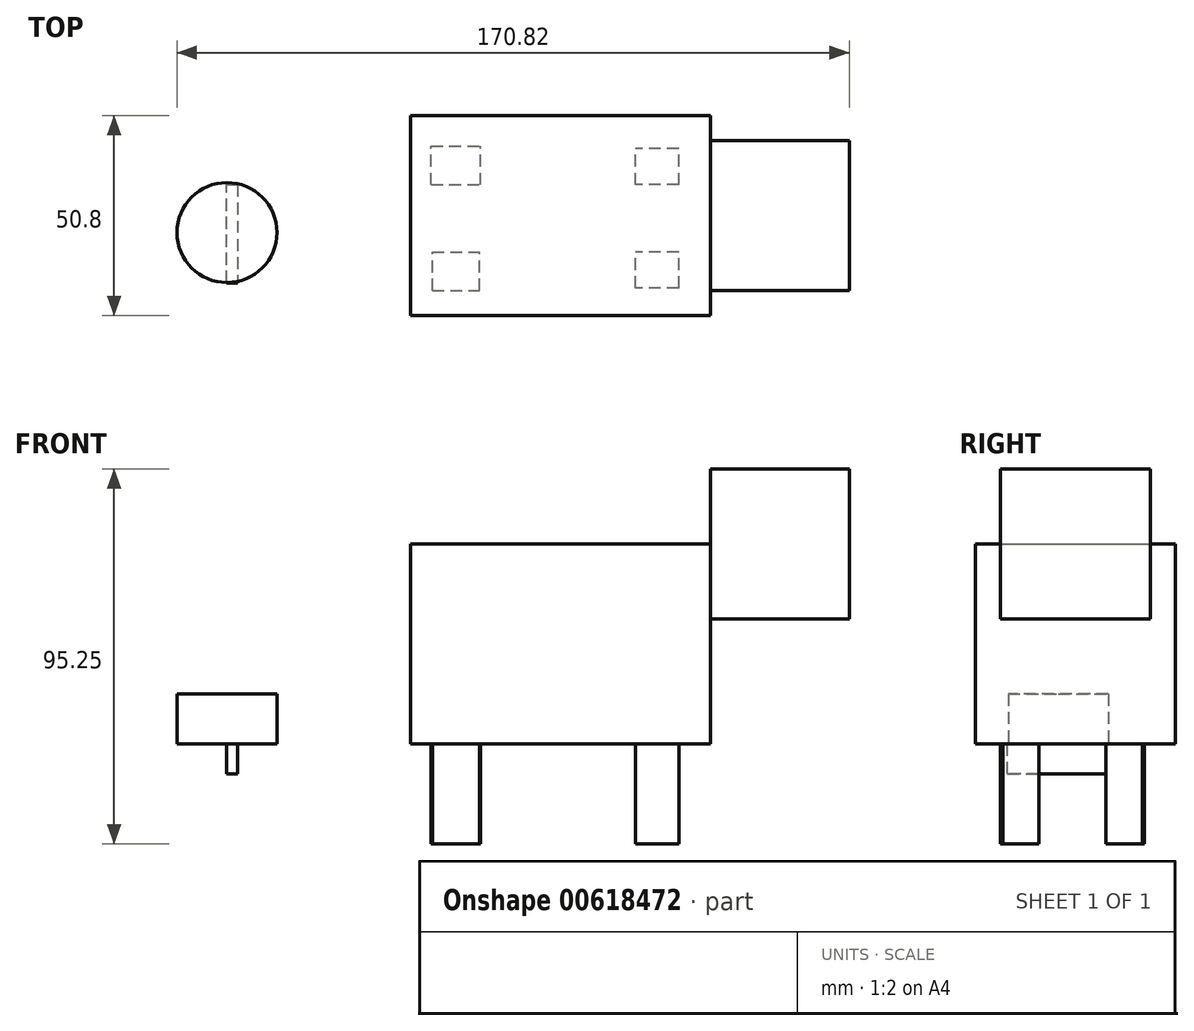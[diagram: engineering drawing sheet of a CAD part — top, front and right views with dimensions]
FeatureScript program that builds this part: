
annotation { "Feature Type Name" : "Feature", "Feature Type Description" : "" }
export const myFeature = defineFeature(function(context is Context, id is Id, definition is map)
    precondition{}
    {
        {
            var Q0;
            Q0=qCreatedBy(makeId("Front.planeOp"),FACE);
            var sketch = newSketch(context, id + "F0", { "sketchPlane" : qUnion([Q0])});
            skLineSegment(sketch, "E0.bottom", {"start": v(-11.56, 59.11) * mm, "end": v(64.64, 59.11) * mm});
            skLineSegment(sketch, "E0.top", {"start": v(-11.56, 8.31) * mm, "end": v(64.64, 8.31) * mm});
            skLineSegment(sketch, "E0.left", {"start": v(-11.56, 59.11) * mm, "end": v(-11.56, 8.31) * mm});
            skLineSegment(sketch, "E0.right", {"start": v(64.64, 59.11) * mm, "end": v(64.64, 8.31) * mm});
            skSolve(sketch);
        }
        {
            var Q0;
            Q0 = qSketchRegion(id + "F0", true);
            extrude(context, id + "F1", {"entities" : qUnion([Q0]), "depth" : 50.8 * mm, "offsetDistance" : 25.4 * mm});
        }
        {
            var Q0;
            Q0=makeQuery(id+"F1.opExtrude","SWEPT_FACE",FACE,{"disambiguationData":[OSD([sQuery(id+"F0.wireOp",EDGE,"E0.right")])]});
            var sketch = newSketch(context, id + "F2", { "sketchPlane" : qUnion([Q0])});
            skLineSegment(sketch, "E1.bottom", {"start": v(-6.35, 78.16) * mm, "end": v(-44.45, 78.16) * mm});
            skLineSegment(sketch, "E1.top", {"start": v(-6.35, 40.06) * mm, "end": v(-44.45, 40.06) * mm});
            skLineSegment(sketch, "E1.left", {"start": v(-6.35, 78.16) * mm, "end": v(-6.35, 40.06) * mm});
            skLineSegment(sketch, "E1.right", {"start": v(-44.45, 78.16) * mm, "end": v(-44.45, 40.06) * mm});
            skPoint(sketch, "E1.middle", {"position": v(-25.4, 59.11) * mm});
            skSolve(sketch);
        }
        {
            var Q0;
            Q0 = qSketchRegion(id + "F2", true);
            extrude(context, id + "F3", {"entities" : qUnion([Q0]), "operationType" : NewBodyOperationType.ADD, "depth" : 35.3 * mm, "offsetDistance" : 25.4 * mm});
        }
        {
            var Q0;
            Q0=makeQuery(id+"F1.opExtrude","SWEPT_FACE",FACE,{"disambiguationData":[OSD([sQuery(id+"F0.wireOp",EDGE,"E0.top")])]});
            var sketch = newSketch(context, id + "F4", { "sketchPlane" : qUnion([Q0])});
            skLineSegment(sketch, "E2.bottom", {"start": v(-6, 44.43) * mm, "end": v(6, 44.43) * mm});
            skLineSegment(sketch, "E2.top", {"start": v(-6, 34.66) * mm, "end": v(6, 34.66) * mm});
            skLineSegment(sketch, "E2.left", {"start": v(-6, 44.43) * mm, "end": v(-6, 34.66) * mm});
            skLineSegment(sketch, "E2.right", {"start": v(6, 44.43) * mm, "end": v(6, 34.66) * mm});
            skPoint(sketch, "E2.middle", {"position": v(0, 39.55) * mm});
            skLineSegment(sketch, "E3.bottom", {"start": v(-6.3, 17.56) * mm, "end": v(6.3, 17.56) * mm});
            skLineSegment(sketch, "E3.top", {"start": v(-6.3, 7.79) * mm, "end": v(6.3, 7.79) * mm});
            skLineSegment(sketch, "E3.left", {"start": v(-6.3, 17.56) * mm, "end": v(-6.3, 7.79) * mm});
            skLineSegment(sketch, "E3.right", {"start": v(6.3, 17.56) * mm, "end": v(6.3, 7.79) * mm});
            skPoint(sketch, "E3.middle", {"position": v(0, 12.67) * mm});
            skLineSegment(sketch, "E4.bottom", {"start": v(56.61, 43.82) * mm, "end": v(45.62, 43.82) * mm});
            skLineSegment(sketch, "E4.top", {"start": v(56.61, 34.66) * mm, "end": v(45.62, 34.66) * mm});
            skLineSegment(sketch, "E4.left", {"start": v(56.61, 43.82) * mm, "end": v(56.61, 34.66) * mm});
            skLineSegment(sketch, "E4.right", {"start": v(45.62, 43.82) * mm, "end": v(45.62, 34.66) * mm});
            skPoint(sketch, "E4.middle", {"position": v(51.12, 39.24) * mm});
            skLineSegment(sketch, "E5.bottom", {"start": v(56.61, 17.56) * mm, "end": v(45.62, 17.56) * mm});
            skLineSegment(sketch, "E5.top", {"start": v(56.61, 8.4) * mm, "end": v(45.62, 8.4) * mm});
            skLineSegment(sketch, "E5.left", {"start": v(56.61, 17.56) * mm, "end": v(56.61, 8.4) * mm});
            skLineSegment(sketch, "E5.right", {"start": v(45.62, 17.56) * mm, "end": v(45.62, 8.4) * mm});
            skPoint(sketch, "E5.middle", {"position": v(51.12, 12.98) * mm});
            skSolve(sketch);
        }
        {
            var Q0;
            Q0 = qSketchRegion(id + "F4", true);
            extrude(context, id + "F5", {"entities" : qUnion([Q0]), "operationType" : NewBodyOperationType.ADD, "depth" : 25.4 * mm, "offsetDistance" : 25.4 * mm});
        }
        {
            var Q0;
            Q0=makeQuery(id+"F1.opExtrude","SWEPT_FACE",FACE,{"disambiguationData":[OSD([sQuery(id+"F0.wireOp",EDGE,"E0.top")])]});
            var sketch = newSketch(context, id + "F6", { "sketchPlane" : qUnion([Q0])});
            skPoint(sketch, "E6", {"position": v(23.62, 26.44) * mm});
            skCircle(sketch, "E7", {"center": v(23.62, 26.44) * mm, "radius": 12.7 * mm});
            skCircle(sketch, "E8", {"center": v(-58.17, 29.72) * mm, "radius": 12.7 * mm});
            skLineSegment(sketch, "E9", {"start": v(-49.3, 38.81) * mm, "end": v(-67, 20.59) * mm});
            skSolve(sketch);
        }
        {
            var Q0;
            {var subQ0=sQuery(id+"F6.wireOp",EDGE,"E9");Q0=makeQuery(id+"F6.imprint","IMPRINT",FACE,{"disambiguationData":[TD([[makeQuery(id+"F6.imprint","IMPRINT",EDGE,{"derivedFrom":subQ0}),-1.0]])]});}
            var Q1;
            {var subQ0=sQuery(id+"F6.wireOp",EDGE,"E9");Q1=makeQuery(id+"F6.imprint","IMPRINT",FACE,{"disambiguationData":[TD([[makeQuery(id+"F6.imprint","IMPRINT",EDGE,{"derivedFrom":subQ0}),1.0]])]});}
            var Q2;
            Q2=makeQuery(id+"F6.imprint","IMPRINT",FACE,{"disambiguationData":[TD([[makeQuery(id+"F6.imprint","IMPRINT",EDGE,{"derivedFrom":sQuery(id+"F6.wireOp",EDGE,"E7")}),1.0]])]});
            extrude(context, id + "F7", {"entities" : qUnion([Q0, Q1, Q2]), "operationType" : NewBodyOperationType.ADD, "depth" : -12.7 * mm, "offsetDistance" : 25.4 * mm});
        }
        {
            var Q0;
            Q0=makeQuery(id+"F7.opExtrude","CAP_FACE",FACE,{"disambiguationData":[OSD([sQuery(id+"F6.wireOp",EDGE,"E8")])],"isStart":true});
            var sketch = newSketch(context, id + "F8", { "sketchPlane" : qUnion([Q0])});
            skLineSegment(sketch, "E10", {"start": v(-58.22, 42.42) * mm, "end": v(-58.22, 17.02) * mm});
            skSolve(sketch);
        }
        {
            var Q0;
            Q0=makeQuery(id+"F6.imprint","IMPRINT",FACE,{"disambiguationData":[TD([[makeQuery(id+"F6.imprint","IMPRINT",EDGE,{"derivedFrom":sQuery(id+"F6.wireOp",EDGE,"E7")}),1.0]])]});
            extrude(context, id + "F9", {"entities" : qUnion([Q0]), "operationType" : NewBodyOperationType.ADD, "depth" : -12.7 * mm, "offsetDistance" : 25.4 * mm});
        }
        {
            var Q0;
            {var subQ0=sQuery(id+"F8.wireOp",EDGE,"E10");Q0=makeQuery(id+"F8.imprint","IMPRINT",FACE,{"disambiguationData":[TD([[makeQuery(id+"F8.imprint","IMPRINT",EDGE,{"derivedFrom":subQ0}),1.0]])]});}
            var sketch = newSketch(context, id + "F10", { "sketchPlane" : qUnion([Q0])});
            skLineSegment(sketch, "E11", {"start": v(-58.21, 42.6) * mm, "end": v(-58.21, 17.56) * mm});
            skLineSegment(sketch, "E12", {"start": v(-58.21, 17.56) * mm, "end": v(-55.46, 17.56) * mm});
            skLineSegment(sketch, "E13", {"start": v(-55.46, 17.56) * mm, "end": v(-55.46, 42.6) * mm});
            skLineSegment(sketch, "E14", {"start": v(-55.46, 42.6) * mm, "end": v(-58.21, 42.6) * mm});
            skSolve(sketch);
        }
        {
            var Q0;
            Q0 = qSketchRegion(id + "F10", true);
            extrude(context, id + "F11", {"entities" : qUnion([Q0]), "operationType" : NewBodyOperationType.ADD, "depth" : 7.62 * mm, "offsetDistance" : 25.4 * mm});
        }
        {
            var Q0;
            Q0=makeQuery(id+"F6.imprint","IMPRINT",FACE,{"disambiguationData":[TD([[makeQuery(id+"F6.imprint","IMPRINT",EDGE,{"derivedFrom":sQuery(id+"F6.wireOp",EDGE,"E7")}),1.0]])]});
            extrude(context, id + "F12", {"entities" : qUnion([Q0]), "operationType" : NewBodyOperationType.ADD, "depth" : -25.4 * mm, "offsetDistance" : 25.4 * mm});
        }
    });
